# Revit family: Specialty_Equipment-Planter-Planters_Unlimited-Ashville-Square-Rectangular
name_source: partatom
category: Specialty Equipment
units: mm (PartAtom-declared; Revit-internal decimal feet)

## family parameters
Always vertical = Yes
Cut with Voids When Loaded = No
Enable Cutting in Views = Yes
Maintain Annotation Orientation = No
OmniClass Number = 23.40.05.21.17
OmniClass Title = Planters
Part Type = Normal
Room Calculation Point = No
Round Connector Dimension = Use Diameter
Shared = No
Work Plane-Based = No

## types (1)
- Default - Load Type Catalog
    3 Pads Rectangle Planter = No
    4 Pads Rectangle Planter = Yes
    Assembly Code = G2050600
    CD_Height = 12"
    CD_Height Max = 36"
    CD_Height Min = 12"
    CD_Length = 18"
    CD_Length Max = 72"
    CD_Length Min = 18"
    CD_Offset = 5"
    CD_Product Name = Ashville Planter
    CD_Product Page URL = https://www.plantersunlimited.com
    CD_Requested Height = 12"
    CD_Requested Length = 18"
    CD_Requested Length Bottom = 12"
    CD_Requested Width = 12"
    CD_Requested Width Bottom = 8"
    CD_Specification = https://www.plantersunlimited.com
    CD_Width = 12"
    CD_Width Max = 72"
    CD_Width Min = 12"
    Center Divider = No
    Center Divider Visibility by Length = No
    Corner Support = No
    Corner Support Visibility by Length = No
    Default Elevation = 0"
    Description = Modular Planting Bed
    Double Panel = No
    Manufacturer = Planters Unlimited
    Material = Plastic-Fiberglass-Carlsbad-Semi_Gloss-Charcoal
    Model = Ashville Series Planters
    Rectangle Planter = Yes
    Single Panel = Yes
    Square Planter = No
    Stiffeners Horizontal = Yes
    Type Comments = Rectangular/Square Planter
    URL = https://www.plantersunlimited.com

## geometry (parser evidence)
native form markers: Extrusion x5, Sweep x2
no freeform markers — native parametric forms only
